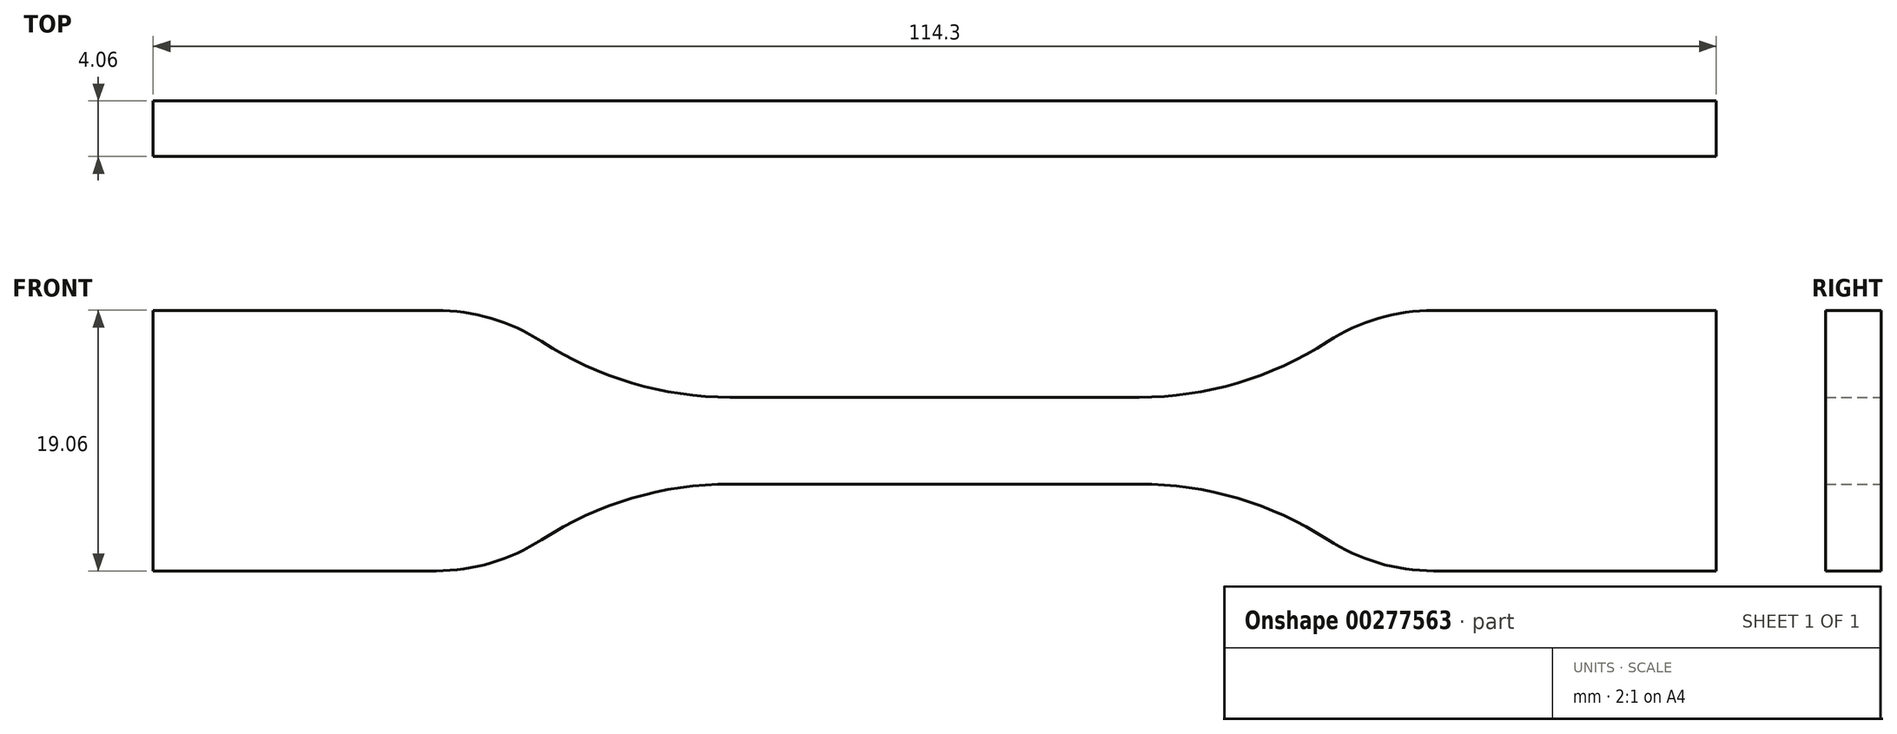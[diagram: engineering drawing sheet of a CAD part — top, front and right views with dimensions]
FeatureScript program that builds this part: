
annotation { "Feature Type Name" : "Feature", "Feature Type Description" : "" }
export const myFeature = defineFeature(function(context is Context, id is Id, definition is map)
    precondition{}
    {
        {
            var Q0;
            Q0=qCreatedBy(makeId("Front.planeOp"),FACE);
            var sketch = newSketch(context, id + "F0", { "sketchPlane" : qUnion([Q0])});
            skLineSegment(sketch, "E0", {"start": v(0, 3.17) * mm, "end": v(14.95, 3.17) * mm});
            skArc(sketch, "E1", {"start": v(14.95, 3.18) * mm, "mid": v(22.14, 4.21) * mm, "end": v(28.74, 7.25) * mm});
            skLineSegment(sketch, "E2", {"start": v(36.46, 9.53) * mm, "end": v(57.15, 9.53) * mm});
            skLineSegment(sketch, "E3", {"start": v(57.15, 9.53) * mm, "end": v(57.15, 0) * mm});
            skLineSegment(sketch, "E4.MirrorCS", {"start": v(0, -3.18) * mm, "end": v(14.95, -3.18) * mm});
            skLineSegment(sketch, "E5.MirrorCS", {"start": v(57.15, -9.53) * mm, "end": v(57.15, 0) * mm});
            skLineSegment(sketch, "E6.MirrorCS", {"start": v(36.46, -9.53) * mm, "end": v(57.15, -9.53) * mm});
            skArc(sketch, "E7.MirrorCS", {"start": v(14.95, -3.18) * mm, "mid": v(22.14, -4.21) * mm, "end": v(28.74, -7.25) * mm});
            skArc(sketch, "E8.MirrorCS", {"start": v(-14.95, -3.18) * mm, "mid": v(-22.14, -4.21) * mm, "end": v(-28.74, -7.25) * mm});
            skLineSegment(sketch, "E9.MirrorCS", {"start": v(-36.46, -9.53) * mm, "end": v(-57.15, -9.53) * mm});
            skArc(sketch, "E10.MirrorCS", {"start": v(-14.95, 3.18) * mm, "mid": v(-22.14, 4.21) * mm, "end": v(-28.74, 7.25) * mm});
            skLineSegment(sketch, "E11.MirrorCS", {"start": v(-36.46, 9.53) * mm, "end": v(-57.15, 9.53) * mm});
            skLineSegment(sketch, "E12.MirrorCS", {"start": v(-57.15, -9.53) * mm, "end": v(-57.15, 0) * mm});
            skLineSegment(sketch, "E13.MirrorCS", {"start": v(0, -3.18) * mm, "end": v(-14.95, -3.18) * mm});
            skLineSegment(sketch, "E14.MirrorCS", {"start": v(-57.15, 9.53) * mm, "end": v(-57.15, 0) * mm});
            skLineSegment(sketch, "E15.MirrorCS", {"start": v(0, 3.18) * mm, "end": v(-14.95, 3.18) * mm});
            skPoint(sketch, "E16.visualSharp", {"position": v(31.75, 9.53) * mm});
            skArc(sketch, "E16.filletArc", {"start": v(36.46, 9.53) * mm, "mid": v(32.44, 8.94) * mm, "end": v(28.74, 7.25) * mm});
            skPoint(sketch, "E17.visualSharp", {"position": v(-31.75, 9.53) * mm});
            skArc(sketch, "E17.filletArc", {"start": v(-28.74, 7.25) * mm, "mid": v(-32.44, 8.94) * mm, "end": v(-36.46, 9.53) * mm});
            skPoint(sketch, "E18.visualSharp", {"position": v(-31.75, -9.53) * mm});
            skArc(sketch, "E18.filletArc", {"start": v(-36.46, -9.53) * mm, "mid": v(-32.44, -8.94) * mm, "end": v(-28.74, -7.25) * mm});
            skPoint(sketch, "E19.visualSharp", {"position": v(31.75, -9.53) * mm});
            skArc(sketch, "E19.filletArc", {"start": v(28.74, -7.25) * mm, "mid": v(32.44, -8.94) * mm, "end": v(36.46, -9.53) * mm});
            skSolve(sketch);
        }
        {
            var Q0;
            Q0 = qSketchRegion(id + "F0", true);
            extrude(context, id + "F1", {"entities" : qUnion([Q0]), "depth" : 4.06 * mm});
        }
    });
